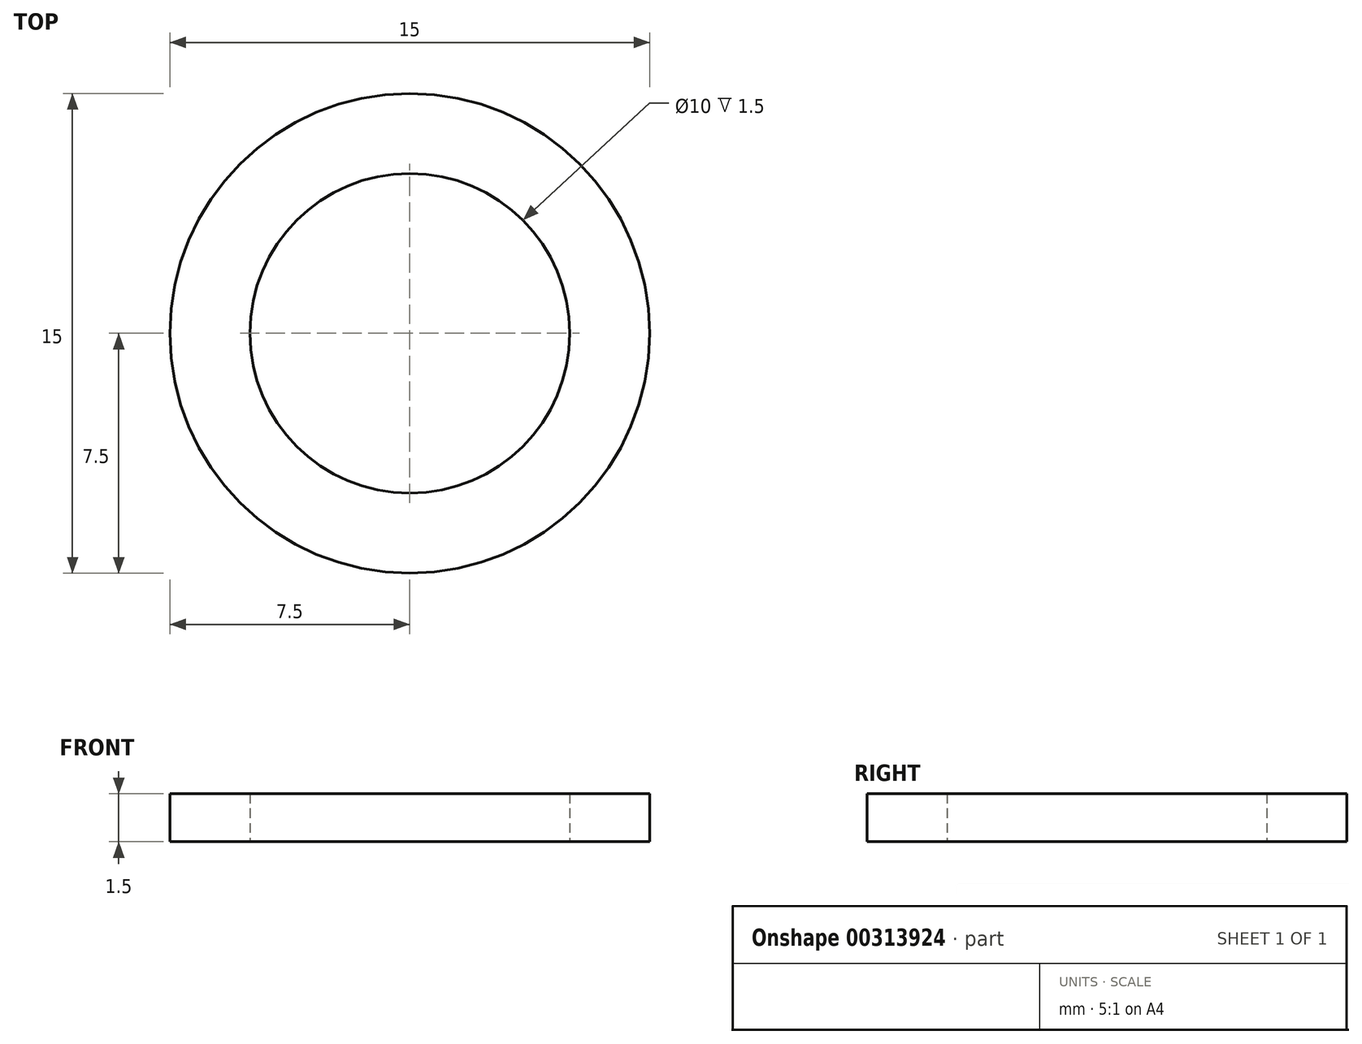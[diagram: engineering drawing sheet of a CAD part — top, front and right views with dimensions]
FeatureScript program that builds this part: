
annotation { "Feature Type Name" : "Feature", "Feature Type Description" : "" }
export const myFeature = defineFeature(function(context is Context, id is Id, definition is map)
    precondition{}
    {
        {
            var Q0;
            Q0=qCreatedBy(makeId("Top.planeOp"),FACE);
            var sketch = newSketch(context, id + "F0", { "sketchPlane" : qUnion([Q0])});
            skCircle(sketch, "E0", {"center": v(0, 0) * mm, "radius": 5 * mm});
            skCircle(sketch, "E1", {"center": v(0, 0) * mm, "radius": 7.5 * mm});
            skSolve(sketch);
        }
        {
            var Q0;
            Q0=makeQuery(id+"F0.imprint","IMPRINT",FACE,{"disambiguationData":[TD([[makeQuery(id+"F0.imprint","IMPRINT",EDGE,{"derivedFrom":sQuery(id+"F0.wireOp",EDGE,"E0")}),-1.0]])]});
            extrude(context, id + "F1", {"entities" : qUnion([Q0]), "depth" : 1.5 * mm});
        }
    });
